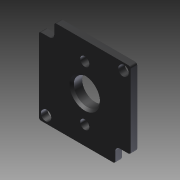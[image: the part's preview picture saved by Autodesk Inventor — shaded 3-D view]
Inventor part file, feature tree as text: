
AUTODESK INVENTOR PART (.ipt)
format: ipt  version: 2014 (Build 180170000, 170)  size: 265,728 bytes
history: native  units: in
note: dims shown in document units (in); Inventor stores cm internally (conversion verified against a paired STEP export)
features: fillet x1, other x1, imported_body x1
ambient origin geometry x8: Origin, YZ Plane, XZ Plane, XY Plane, X Axis, Y Axis, Z Axis, Center Point
bodies: Body1 (feature_tree)
feature tree (3):
  fillet  "Fillet4"  [1 undecoded]
  other  "217-2822-BAG Mounting Plate STEP1"
  imported_body  "Base1"
note: 1 required parameter value undecoded (feature->parameter linkage not recoverable at this tier; creation-order binding heuristic only, values carry confidence <= 0.55)
